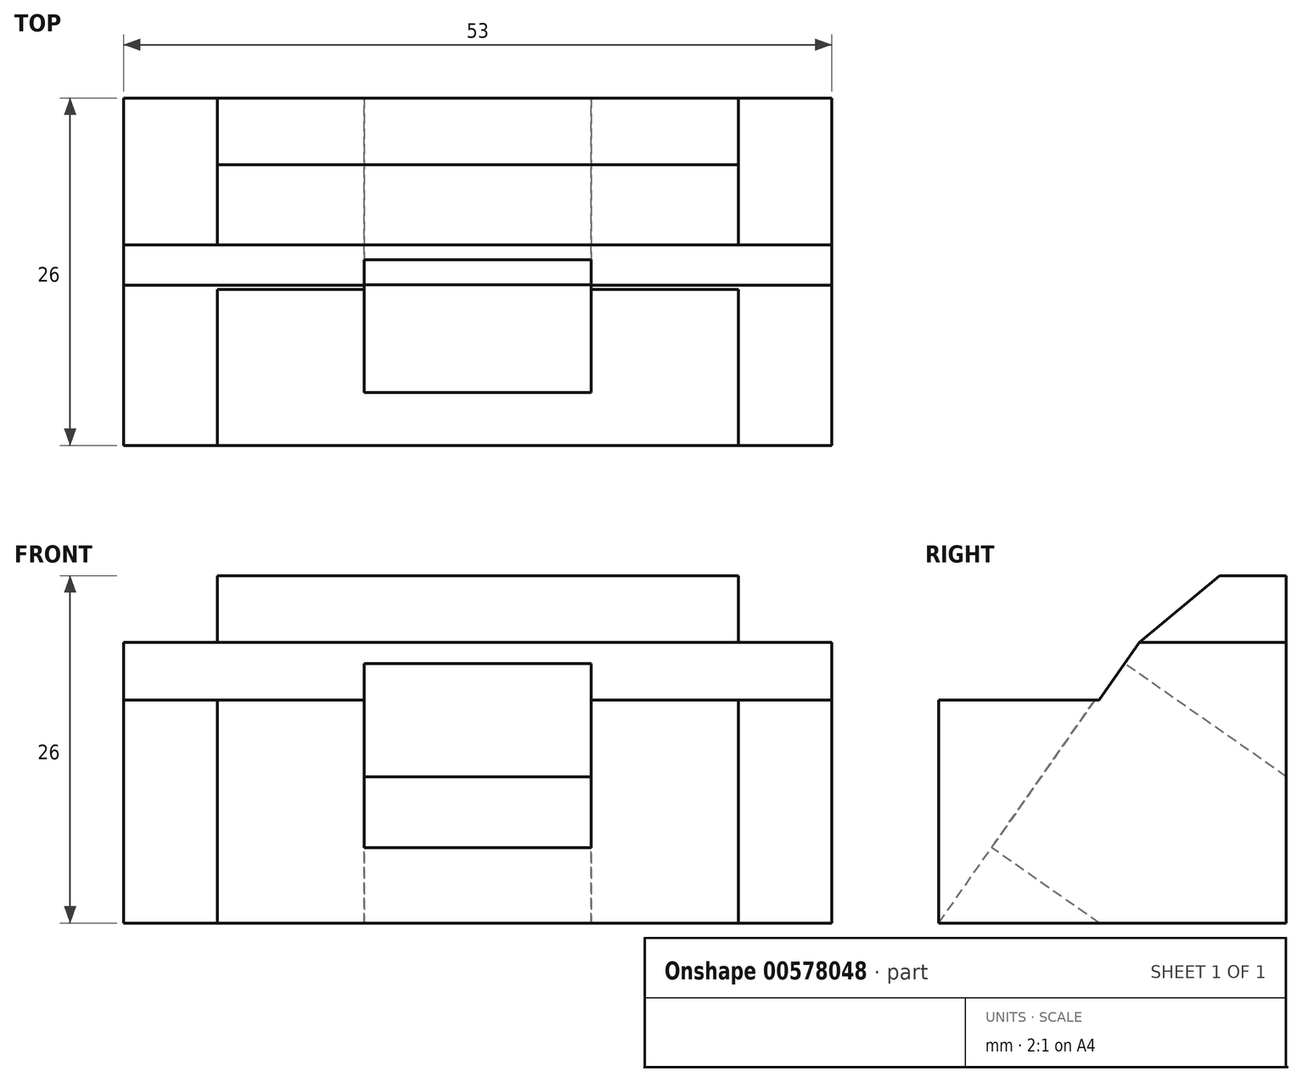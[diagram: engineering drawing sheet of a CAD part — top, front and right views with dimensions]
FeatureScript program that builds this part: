
annotation { "Feature Type Name" : "Feature", "Feature Type Description" : "" }
export const myFeature = defineFeature(function(context is Context, id is Id, definition is map)
    precondition{}
    {
        {
            var Q0;
            Q0=qCreatedBy(makeId("Front.planeOp"),FACE);
            var sketch = newSketch(context, id + "F0", { "sketchPlane" : qUnion([Q0])});
            skLineSegment(sketch, "E0.bottom", {"start": v(26.5, 13) * mm, "end": v(-26.5, 13) * mm});
            skLineSegment(sketch, "E0.top", {"start": v(26.5, -13) * mm, "end": v(-26.5, -13) * mm});
            skLineSegment(sketch, "E0.left", {"start": v(26.5, 13) * mm, "end": v(26.5, -13) * mm});
            skLineSegment(sketch, "E0.right", {"start": v(-26.5, 13) * mm, "end": v(-26.5, -13) * mm});
            skPoint(sketch, "E0.middle", {"position": v(0, 0) * mm});
            skSolve(sketch);
        }
        {
            var Q0;
            Q0=makeQuery(id+"F0.imprint","IMPRINT",FACE,{"disambiguationData":[TD([[makeQuery(id+"F0.imprint","IMPRINT",EDGE,{"derivedFrom":sQuery(id+"F0.wireOp",EDGE,"E0.bottom")}),1.0]])]});
            extrude(context, id + "F1", {"entities" : qUnion([Q0]), "depth" : 26 * mm, "offsetDistance" : 25 * mm});
        }
        {
            var Q0;
            Q0=makeQuery(id+"F1.opExtrude","SWEPT_FACE",FACE,{"disambiguationData":[OSD([sQuery(id+"F0.wireOp",EDGE,"E0.left")])]});
            var sketch = newSketch(context, id + "F2", { "sketchPlane" : qUnion([Q0])});
            skLineSegment(sketch, "E1.bottom", {"start": v(0, 13) * mm, "end": v(-11, 13) * mm});
            skLineSegment(sketch, "E1.top", {"start": v(0, 8) * mm, "end": v(-11, 8) * mm});
            skLineSegment(sketch, "E1.left", {"start": v(0, 13) * mm, "end": v(0, 8) * mm});
            skLineSegment(sketch, "E1.right", {"start": v(-11, 13) * mm, "end": v(-11, 8) * mm});
            skSolve(sketch);
        }
        {
            var Q0;
            Q0 = qSketchRegion(id + "F2", true);
            extrude(context, id + "F3", {"entities" : qUnion([Q0]), "operationType" : NewBodyOperationType.REMOVE, "oppositeDirection" : true, "depth" : 7 * mm, "offsetDistance" : 25 * mm});
        }
        {
            var Q0;
            Q0=makeQuery(id+"F1.opExtrude","SWEPT_FACE",FACE,{"disambiguationData":[OSD([sQuery(id+"F0.wireOp",EDGE,"E0.right")])]});
            var sketch = newSketch(context, id + "F4", { "sketchPlane" : qUnion([Q0])});
            skLineSegment(sketch, "E2.bottom", {"start": v(0, 13) * mm, "end": v(11, 13) * mm});
            skLineSegment(sketch, "E2.top", {"start": v(0, 8) * mm, "end": v(11, 8) * mm});
            skLineSegment(sketch, "E2.left", {"start": v(0, 13) * mm, "end": v(0, 8) * mm});
            skLineSegment(sketch, "E2.right", {"start": v(11, 13) * mm, "end": v(11, 8) * mm});
            skSolve(sketch);
        }
        {
            var Q0;
            Q0 = qSketchRegion(id + "F4", true);
            var Q1;
            Q1=makeQuery(id+"F4.imprint","IMPRINT",FACE,{"disambiguationData":[TD([[makeQuery(id+"F4.imprint","IMPRINT",EDGE,{"derivedFrom":sQuery(id+"F4.wireOp",EDGE,"E2.bottom")}),1.0]])]});
            extrude(context, id + "F5", {"entities" : qUnion([Q0, Q1]), "operationType" : NewBodyOperationType.REMOVE, "oppositeDirection" : true, "depth" : 7 * mm, "offsetDistance" : 25 * mm});
        }
        {
            var Q0;
            Q0=makeQuery(id+"F1.opExtrude","SWEPT_FACE",FACE,{"disambiguationData":[OSD([sQuery(id+"F0.wireOp",EDGE,"E0.left")])]});
            var sketch = newSketch(context, id + "F6", { "sketchPlane" : qUnion([Q0])});
            skLineSegment(sketch, "E3", {"start": v(-26, 13) * mm, "end": v(-20.93, 13) * mm});
            skLineSegment(sketch, "E4", {"start": v(-26, -13) * mm, "end": v(-26, 3.7) * mm});
            skLineSegment(sketch, "E5", {"start": v(-26, 3.7) * mm, "end": v(-14, 3.7) * mm});
            skLineSegment(sketch, "E6", {"start": v(-14, 3.7) * mm, "end": v(-11, 8) * mm});
            skSolve(sketch);
        }
        {
            var Q0;
            {var subQ1=sQuery(id+"F6.wireOp",EDGE,"E3");Q0=makeQuery(id+"F6.imprint","IMPRINT",FACE,{"disambiguationData":[TD([[makeQuery(id+"F6.imprint","IMPRINT",EDGE,{"derivedFrom":subQ1}),-1.0]])]});}
            extrude(context, id + "F7", {"entities" : qUnion([Q0]), "operationType" : NewBodyOperationType.REMOVE, "endBound" : BoundingType.THROUGH_ALL, "oppositeDirection" : true, "depth" : 25 * mm, "offsetDistance" : 25 * mm});
        }
        {
            var Q0;
            Q0=makeQuery(id+"F3.boolean.opBoolean","COPY",FACE,{"derivedFrom":makeQuery(id+"F3.opExtrude","CAP_FACE",FACE,{"disambiguationData":[OSD([sQuery(id+"F2.wireOp",EDGE,"E1.bottom"),sQuery(id+"F2.wireOp",EDGE,"E1.top"),sQuery(id+"F2.wireOp",EDGE,"E1.left"),sQuery(id+"F2.wireOp",EDGE,"E1.right")])],"isStart":false})});
            var sketch = newSketch(context, id + "F8", { "sketchPlane" : qUnion([Q0])});
            skLineSegment(sketch, "E7", {"start": v(-11, 8) * mm, "end": v(-5, 13) * mm});
            skSolve(sketch);
        }
        {
            var Q0;
            {var subQ0=sQuery(id+"F8.wireOp",EDGE,"E7");Q0=makeQuery(id+"F8.imprint","IMPRINT",FACE,{"disambiguationData":[TD([[makeQuery(id+"F8.imprint","IMPRINT",EDGE,{"derivedFrom":subQ0}),1.0]])]});}
            extrude(context, id + "F9", {"entities" : qUnion([Q0]), "operationType" : NewBodyOperationType.REMOVE, "endBound" : BoundingType.THROUGH_ALL, "oppositeDirection" : true, "depth" : 25 * mm, "offsetDistance" : 25 * mm});
        }
        {
            var Q0;
            Q0=makeQuery(id+"F1.opExtrude","SWEPT_FACE",FACE,{"disambiguationData":[OSD([sQuery(id+"F0.wireOp",EDGE,"E0.right")])]});
            cPlane(context, id + "F10", {"entities" : qUnion([Q0]), "cplaneType" : CPlaneType.OFFSET, "offset" : 7 * mm, "oppositeDirection" : true, "width" : 150 * mm, "height" : 150 * mm});
        }
        {
            var Q0;
            Q0=qCreatedBy(id+"F10.planeOp",FACE);
            var sketch = newSketch(context, id + "F11", { "sketchPlane" : qUnion([Q0])});
            skLineSegment(sketch, "E8", {"start": v(26, 3.8) * mm, "end": v(26, -13) * mm});
            skLineSegment(sketch, "E9", {"start": v(26, -13) * mm, "end": v(11.3, 8) * mm});
            skLineSegment(sketch, "E10", {"start": v(11.3, 8) * mm, "end": v(26, 3.8) * mm});
            skSolve(sketch);
        }
        {
            var Q0;
            Q0 = qSketchRegion(id + "F11", true);
            extrude(context, id + "F12", {"entities" : qUnion([Q0]), "operationType" : NewBodyOperationType.REMOVE, "oppositeDirection" : true, "depth" : 39 * mm, "offsetDistance" : 25 * mm});
        }
        {
            var Q0;
            Q0=makeQuery(id+"F12.boolean.opBoolean","COPY",FACE,{"derivedFrom":makeQuery(id+"F12.opExtrude","SWEPT_FACE",FACE,{"disambiguationData":[OSD([sQuery(id+"F11.wireOp",EDGE,"E9")])]})});
            cPlane(context, id + "F13", {"entities" : qUnion([Q0]), "cplaneType" : CPlaneType.OFFSET, "offset" : 0 * mm, "width" : 150 * mm, "height" : 150 * mm});
        }
        {
            var Q0;
            Q0=qCreatedBy(id+"F13.planeOp",FACE);
            var sketch = newSketch(context, id + "F14", { "sketchPlane" : qUnion([Q0])});
            skLineSegment(sketch, "E11", {"start": v(-8.5, -1.67) * mm, "end": v(8.5, -1.67) * mm});
            skLineSegment(sketch, "E12", {"start": v(8.5, -1.67) * mm, "end": v(8.5, -18.67) * mm});
            skLineSegment(sketch, "E13", {"start": v(8.5, -18.67) * mm, "end": v(-8.5, -18.67) * mm});
            skLineSegment(sketch, "E14", {"start": v(-8.5, -1.67) * mm, "end": v(-8.5, -18.67) * mm});
            skSolve(sketch);
        }
        {
            var Q0;
            Q0 = qSketchRegion(id + "F14", true);
            extrude(context, id + "F15", {"entities" : qUnion([Q0]), "operationType" : NewBodyOperationType.REMOVE, "endBound" : BoundingType.THROUGH_ALL, "oppositeDirection" : true, "depth" : 25 * mm, "offsetDistance" : 25 * mm});
        }
        {
            var Q0;
            Q0 = qSketchRegion(id + "F11", true);
            extrude(context, id + "F16", {"entities" : qUnion([Q0]), "operationType" : NewBodyOperationType.REMOVE, "oppositeDirection" : true, "depth" : 39 * mm, "offsetDistance" : 25 * mm});
        }
    });
